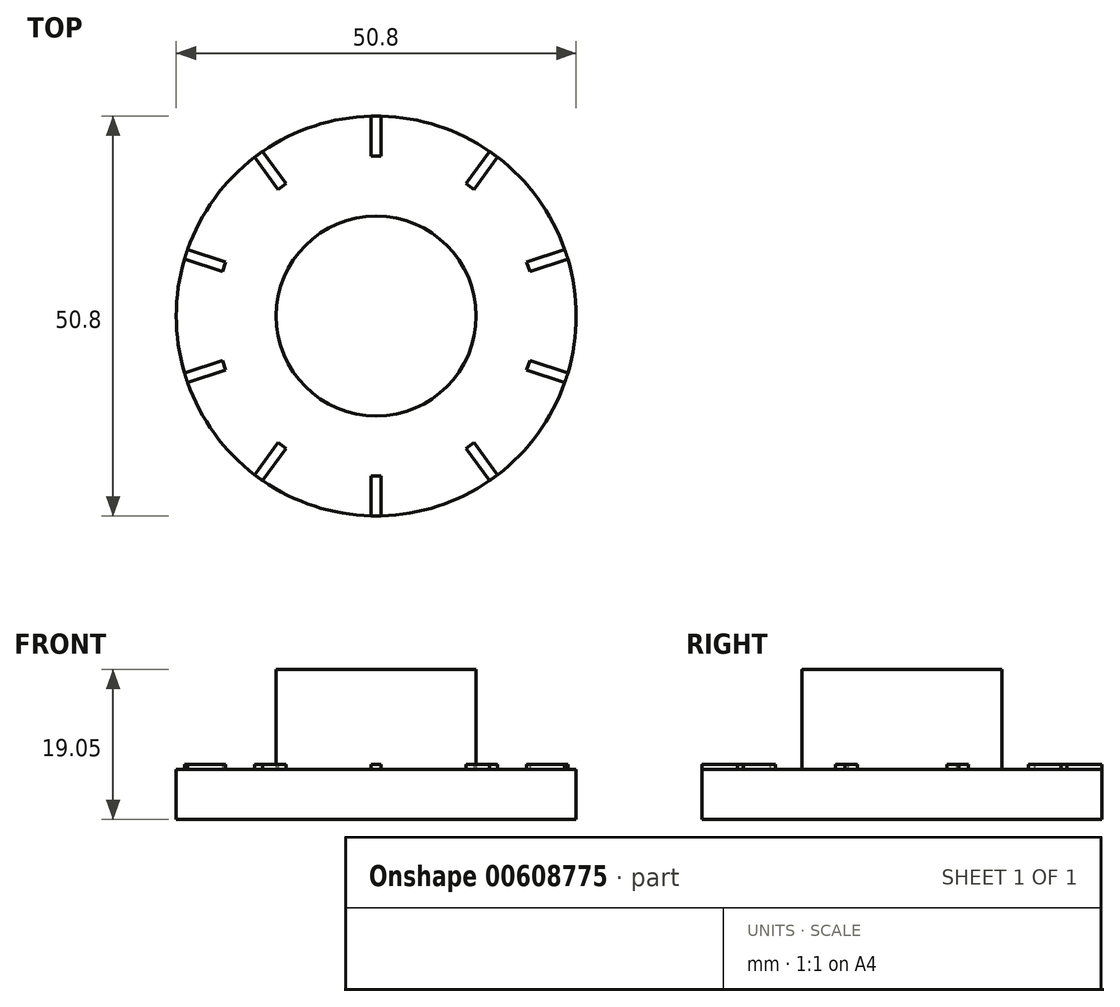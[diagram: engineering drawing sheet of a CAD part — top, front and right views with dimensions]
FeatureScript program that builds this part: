
annotation { "Feature Type Name" : "Feature", "Feature Type Description" : "" }
export const myFeature = defineFeature(function(context is Context, id is Id, definition is map)
    precondition{}
    {
        {
            var Q0;
            Q0=qCreatedBy(makeId("Top.planeOp"),FACE);
            var sketch = newSketch(context, id + "F0", { "sketchPlane" : qUnion([Q0])});
            skCircle(sketch, "E0", {"center": v(0, 0) * mm, "radius": 25.4 * mm});
            skSolve(sketch);
        }
        {
            var Q0;
            Q0=makeQuery(id+"F0.imprint","IMPRINT",FACE,{"disambiguationData":[TD([[makeQuery(id+"F0.imprint","IMPRINT",EDGE,{"derivedFrom":sQuery(id+"F0.wireOp",EDGE,"E0")}),1.0]])]});
            extrude(context, id + "F1", {"entities" : qUnion([Q0]), "depth" : 6.35 * mm, "offsetDistance" : 25.4 * mm});
        }
        {
            var Q0;
            Q0=makeQuery(id+"F1.opExtrude","CAP_FACE",FACE,{"disambiguationData":[OSD([sQuery(id+"F0.wireOp",EDGE,"E0")])],"isStart":false});
            var sketch = newSketch(context, id + "F2", { "sketchPlane" : qUnion([Q0])});
            skCircle(sketch, "E1", {"center": v(0, 0) * mm, "radius": 12.7 * mm});
            skSolve(sketch);
        }
        {
            var Q0;
            Q0=makeQuery(id+"F2.imprint","IMPRINT",FACE,{"disambiguationData":[TD([[makeQuery(id+"F2.imprint","IMPRINT",EDGE,{"derivedFrom":sQuery(id+"F2.wireOp",EDGE,"E1")}),-1.0]])]});
            var sketch = newSketch(context, id + "F3", { "sketchPlane" : qUnion([Q0])});
            skLineSegment(sketch, "E2", {"start": v(0.64, 25.4) * mm, "end": v(0.64, 20.31) * mm});
            skLineSegment(sketch, "E3", {"start": v(0.63, 20.31) * mm, "end": v(-0.64, 20.31) * mm});
            skLineSegment(sketch, "E4", {"start": v(-0.64, 20.31) * mm, "end": v(-0.64, 25.4) * mm});
            skSolve(sketch);
        }
        {
            var Q0;
            {var subQ0=sQuery(id+"F3.wireOp",EDGE,"E2");Q0=makeQuery(id+"F3.imprint","IMPRINT",FACE,{"disambiguationData":[TD([[makeQuery(id+"F3.imprint","IMPRINT",EDGE,{"derivedFrom":subQ0}),-1.0]])]});}
            extrude(context, id + "F4", {"entities" : qUnion([Q0]), "operationType" : NewBodyOperationType.ADD, "depth" : 0.64 * mm, "offsetDistance" : 25.4 * mm});
        }
        {
            var Q0;
            Q0=makeQuery(id+"F2.imprint","IMPRINT",FACE,{"disambiguationData":[TD([[makeQuery(id+"F2.imprint","IMPRINT",EDGE,{"derivedFrom":sQuery(id+"F2.wireOp",EDGE,"E1")}),1.0]])]});
            extrude(context, id + "F5", {"entities" : qUnion([Q0]), "operationType" : NewBodyOperationType.ADD, "depth" : 12.7 * mm, "offsetDistance" : 25.4 * mm});
        }
        {
            var Q0;
            Q0=makeQuery(id+"F1.opExtrude","SWEPT_BODY",BODY,{"disambiguationData":[OSD([sQuery(id+"F0.wireOp",EDGE,"E0")])]});
            var Q1;
            Q1=makeQuery(id+"F5.opExtrude","SWEPT_FACE",FACE,{"disambiguationData":[OSD([sQuery(id+"F2.wireOp",EDGE,"E1")])]});
            circularPattern(context, id + "F6", {"entities" : qUnion([Q0]), "axis" : qUnion([Q1]), "angle" : 360 * degree, "instanceCount" : 10, "equalSpace" : true});
        }
    });
